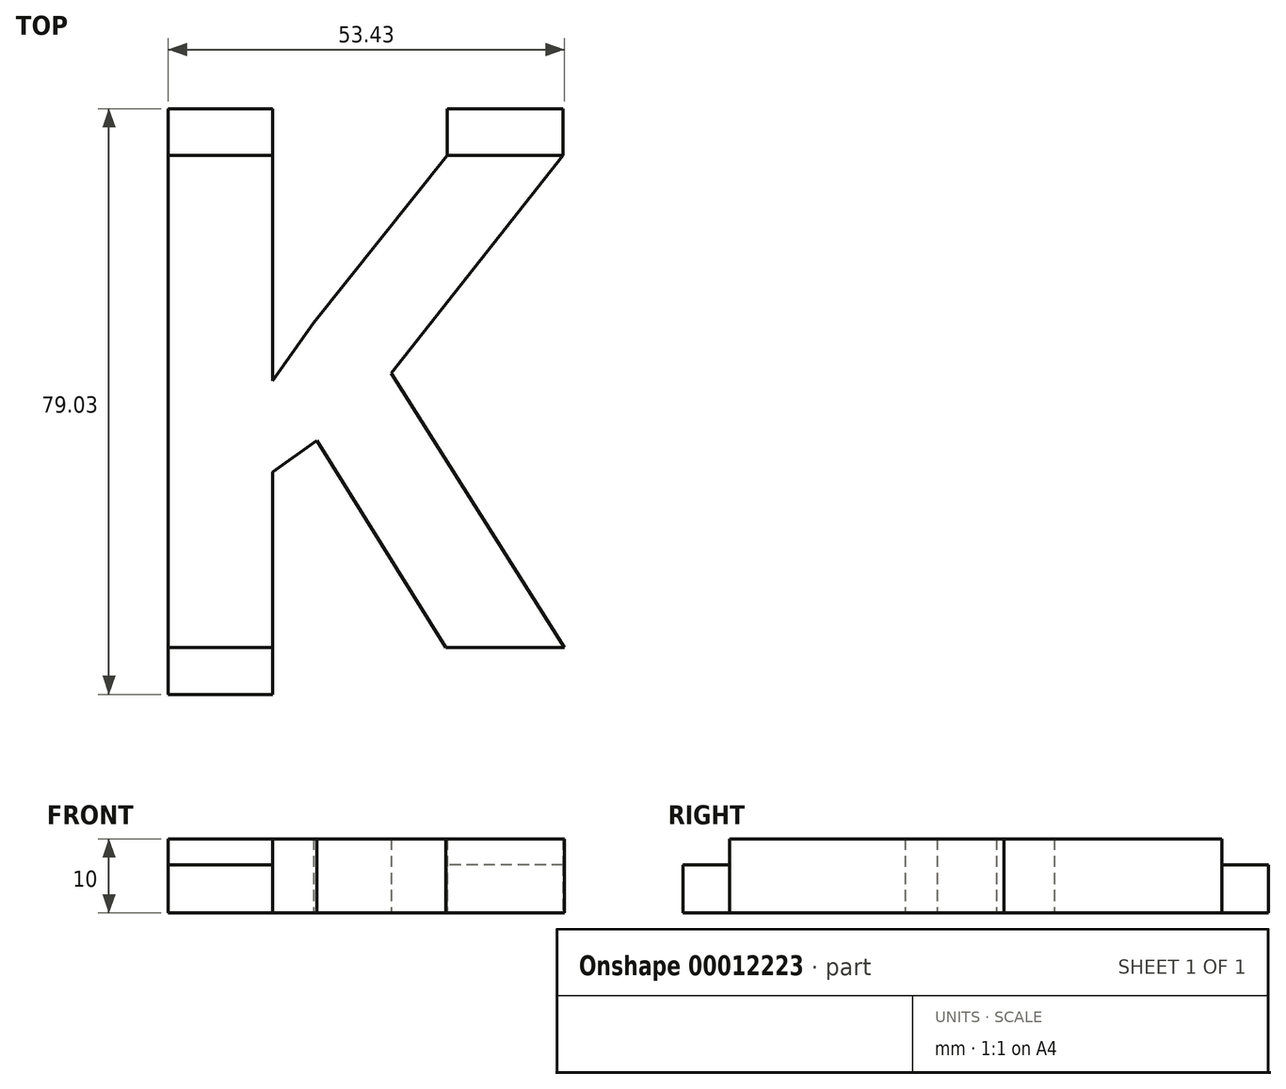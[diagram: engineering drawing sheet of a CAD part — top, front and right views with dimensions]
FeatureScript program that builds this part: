
annotation { "Feature Type Name" : "Feature", "Feature Type Description" : "" }
export const myFeature = defineFeature(function(context is Context, id is Id, definition is map)
    precondition{}
    {
        {
            var Q0;
            Q0=qCreatedBy(makeId("Top.planeOp"),FACE);
            var sketch = newSketch(context, id + "F0", { "sketchPlane" : qUnion([Q0])});
            skText(sketch, "E0", { "text": "K", "fontName": "OpenSans-Bold.ttf"});
            const initialGuessF0  = {"E0": [-0.0618, 0, 1, 0, 0.067]};
            skSetInitialGuess(sketch, initialGuessF0);
            skSolve(sketch);
        }
        {
            var Q0;
            Q0=makeQuery(id+"F0.imprint","IMPRINT",FACE,{"disambiguationData":[TD([[makeQuery(id+"F0.imprint","IMPRINT",EDGE,{"derivedFrom":sQuery(id+"F0.wireOp",EDGE,"E0.sketch_text.stroke-0")}),-1.0]])]});
            extrude(context, id + "F1", {"entities" : qUnion([Q0]), "depth" : 10 * mm});
        }
        {
            var Q0;
            Q0=makeQuery(id+"F1.opExtrude","SWEPT_FACE",FACE,{"disambiguationData":[OSD([sQuery(id+"F0.wireOp",EDGE,"E0.sketch_text.stroke-4")])]});
            var sketch = newSketch(context, id + "F2", { "sketchPlane" : qUnion([Q0])});
            skLineSegment(sketch, "E1.0.0", {"start": v(-53.43, 0) * mm, "end": v(-39.35, 0) * mm});
            skLineSegment(sketch, "E1.0.1", {"start": v(-39.35, 0) * mm, "end": v(-39.35, 10) * mm});
            skLineSegment(sketch, "E1.0.2", {"start": v(-39.35, 10) * mm, "end": v(-53.43, 10) * mm});
            skLineSegment(sketch, "E1.0.3", {"start": v(-53.43, 10) * mm, "end": v(-53.43, 0) * mm});
            skLineSegment(sketch, "E2.top", {"start": v(-53.43, 6.5) * mm, "end": v(-39.35, 6.5) * mm});
            skLineSegment(sketch, "E2.left", {"start": v(-53.43, 0) * mm, "end": v(-53.43, 6.5) * mm});
            skLineSegment(sketch, "E2.right", {"start": v(-39.35, 0) * mm, "end": v(-39.35, 6.5) * mm});
            skLineSegment(sketch, "E3.0.0", {"start": v(-16, 0) * mm, "end": v(0, 0) * mm});
            skLineSegment(sketch, "E3.0.1", {"start": v(0, 0) * mm, "end": v(0, 10) * mm});
            skLineSegment(sketch, "E3.0.2", {"start": v(0, 10) * mm, "end": v(-16, 10) * mm});
            skLineSegment(sketch, "E3.0.3", {"start": v(-16, 10) * mm, "end": v(-16, 0) * mm});
            skLineSegment(sketch, "E4.bottom", {"start": v(0, 0) * mm, "end": v(-16, 0) * mm});
            skLineSegment(sketch, "E4.top", {"start": v(0, 6.5) * mm, "end": v(-16, 6.5) * mm});
            skLineSegment(sketch, "E4.left", {"start": v(0, 0) * mm, "end": v(0, 6.5) * mm});
            skLineSegment(sketch, "E4.right", {"start": v(-16, 0) * mm, "end": v(-16, 6.5) * mm});
            skSolve(sketch);
        }
        {
            var Q0;
            Q0=makeQuery(id+"F2.imprint","IMPRINT",FACE,{"disambiguationData":[TD([[makeQuery(id+"F2.imprint","IMPRINT",EDGE,{"derivedFrom":sQuery(id+"F2.wireOp",EDGE,"E1.0.0")}),-1.0]])]});
            var Q1;
            Q1=makeQuery(id+"F2.imprint","IMPRINT",FACE,{"disambiguationData":[TD([[makeQuery(id+"F2.imprint","IMPRINT",EDGE,{"derivedFrom":sQuery(id+"F2.wireOp",EDGE,"E4.bottom")}),-1.0]])]});
            extrude(context, id + "F3", {"entities" : qUnion([Q0, Q1]), "operationType" : NewBodyOperationType.ADD, "depth" : 6.3 * mm});
        }
        {
            var Q0;
            Q0=makeQuery(id+"F1.opExtrude","SWEPT_FACE",FACE,{"disambiguationData":[OSD([sQuery(id+"F0.wireOp",EDGE,"E0.sketch_text.stroke-10")])]});
            var sketch = newSketch(context, id + "F4", { "sketchPlane" : qUnion([Q0])});
            skLineSegment(sketch, "E5.0.0", {"start": v(0.17, 0) * mm, "end": v(15.8, 0) * mm});
            skLineSegment(sketch, "E5.0.1", {"start": v(15.8, 0) * mm, "end": v(15.8, 10) * mm});
            skLineSegment(sketch, "E5.0.2", {"start": v(15.8, 10) * mm, "end": v(0.17, 10) * mm});
            skLineSegment(sketch, "E5.0.3", {"start": v(0.17, 10) * mm, "end": v(0.17, 0) * mm});
            skLineSegment(sketch, "E6.top", {"start": v(0.17, 6.5) * mm, "end": v(15.8, 6.5) * mm});
            skLineSegment(sketch, "E6.left", {"start": v(0.17, 0) * mm, "end": v(0.17, 6.5) * mm});
            skLineSegment(sketch, "E6.right", {"start": v(15.8, 0) * mm, "end": v(15.8, 6.5) * mm});
            skLineSegment(sketch, "E7.0.0", {"start": v(39.35, 0) * mm, "end": v(53.43, 0) * mm});
            skLineSegment(sketch, "E7.0.1", {"start": v(53.43, 0) * mm, "end": v(53.43, 10) * mm});
            skLineSegment(sketch, "E7.0.2", {"start": v(53.43, 10) * mm, "end": v(39.35, 10) * mm});
            skLineSegment(sketch, "E7.0.3", {"start": v(39.35, 10) * mm, "end": v(39.35, 0) * mm});
            skLineSegment(sketch, "E8.top", {"start": v(39.35, 6.5) * mm, "end": v(53.43, 6.5) * mm});
            skLineSegment(sketch, "E8.left", {"start": v(39.35, 0) * mm, "end": v(39.35, 6.5) * mm});
            skLineSegment(sketch, "E8.right", {"start": v(53.43, 0) * mm, "end": v(53.43, 6.5) * mm});
            skSolve(sketch);
        }
        {
            var Q0;
            Q0=makeQuery(id+"F4.imprint","IMPRINT",FACE,{"disambiguationData":[TD([[makeQuery(id+"F4.imprint","IMPRINT",EDGE,{"derivedFrom":sQuery(id+"F4.wireOp",EDGE,"E5.0.0")}),-1.0]])]});
            var Q1;
            Q1=makeQuery(id+"F4.imprint","IMPRINT",FACE,{"disambiguationData":[TD([[makeQuery(id+"F4.imprint","IMPRINT",EDGE,{"derivedFrom":sQuery(id+"F4.wireOp",EDGE,"E7.0.0")}),1.0]])]});
            extrude(context, id + "F5", {"entities" : qUnion([Q0, Q1]), "operationType" : NewBodyOperationType.ADD, "depth" : 6.3 * mm});
        }
    });
